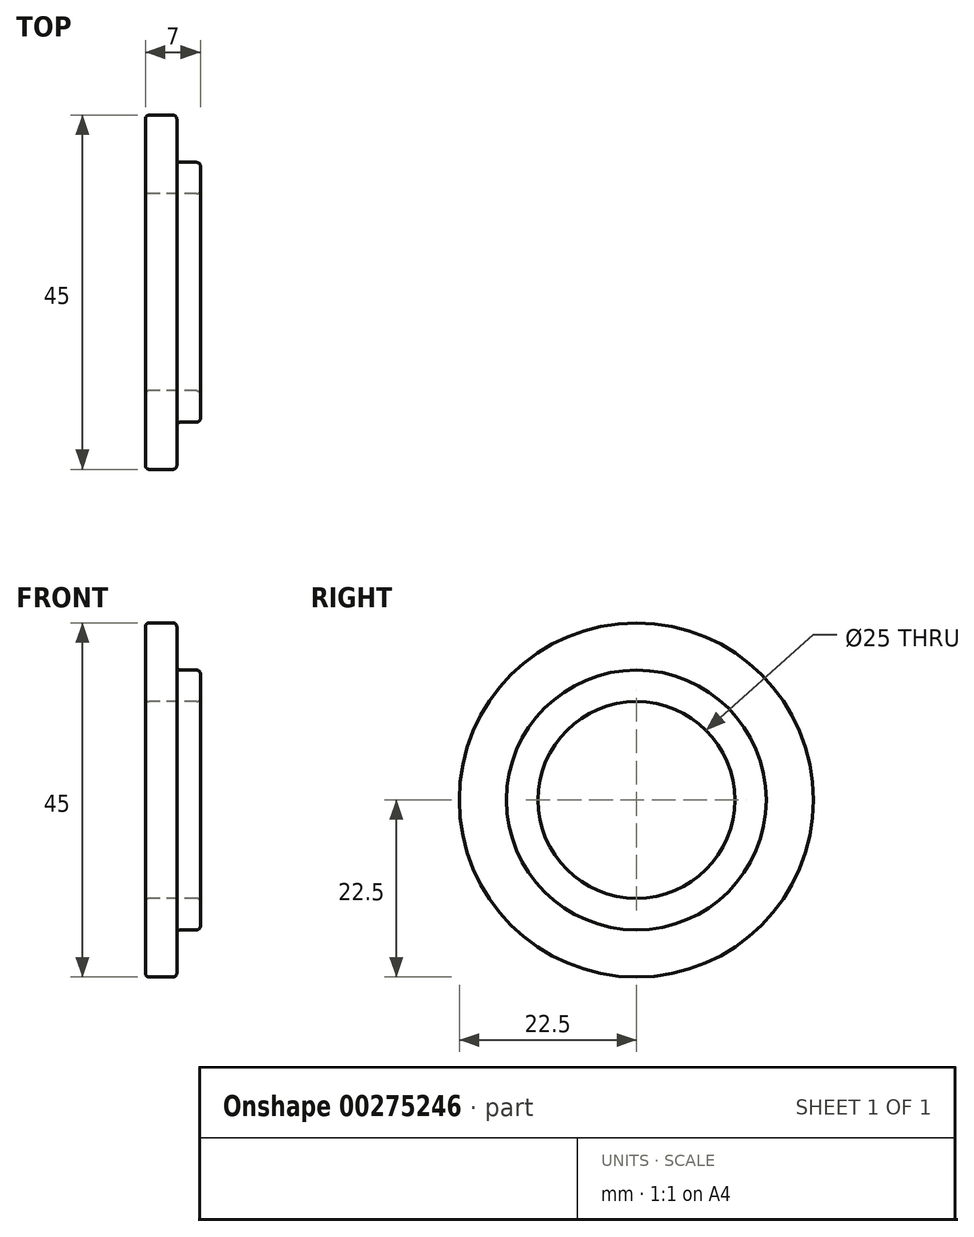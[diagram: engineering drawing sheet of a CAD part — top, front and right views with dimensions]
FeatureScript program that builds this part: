
annotation { "Feature Type Name" : "Feature", "Feature Type Description" : "" }
export const myFeature = defineFeature(function(context is Context, id is Id, definition is map)
    precondition{}
    {
        {
            var Q0;
            Q0=qCreatedBy(makeId("Front.planeOp"),FACE);
            var sketch = newSketch(context, id + "F0", { "sketchPlane" : qUnion([Q0])});
            skLineSegment(sketch, "E0", {"start": v(0, 0) * mm, "end": v(0, 10) * mm});
            skLineSegment(sketch, "E1", {"start": v(0, 10) * mm, "end": v(4, 10) * mm});
            skLineSegment(sketch, "E2", {"start": v(4, 10) * mm, "end": v(4, 4) * mm});
            skLineSegment(sketch, "E3", {"start": v(4, 4) * mm, "end": v(7, 4) * mm});
            skLineSegment(sketch, "E4", {"start": v(7, 4) * mm, "end": v(7, 0) * mm});
            skLineSegment(sketch, "E5", {"start": v(7, 0) * mm, "end": v(0, 0) * mm});
            skLineSegment(sketch, "E6", {"start": v(-26.03, -12.5) * mm, "end": v(32.28, -12.5) * mm, "construction": true});
            skSolve(sketch);
        }
        {
            var Q0;
            Q0 = qSketchRegion(id + "F0", true);
            var Q1;
            Q1=sQuery(id+"F0.wireOp",EDGE,"E6");
            revolve(context, id + "F1", {"entities" : qUnion([Q0]), "axis" : qUnion([Q1]), "revolveType" : RevolveType.FULL});
        }
        {
            var Q0;
            Q0=makeQuery(id+"F1.opRevolve","SWEPT_EDGE",EDGE,{"disambiguationData":[OSD([sQuery(id+"F0.wireOp",EDGE,"E3"),sQuery(id+"F0.wireOp",EDGE,"E4")])]});
            var Q1;
            Q1=makeQuery(id+"F1.opRevolve","SWEPT_EDGE",EDGE,{"disambiguationData":[OSD([sQuery(id+"F0.wireOp",EDGE,"E4"),sQuery(id+"F0.wireOp",EDGE,"E5")])]});
            var Q2;
            Q2=makeQuery(id+"F1.opRevolve","SWEPT_EDGE",EDGE,{"disambiguationData":[OSD([sQuery(id+"F0.wireOp",EDGE,"E1"),sQuery(id+"F0.wireOp",EDGE,"E2")])]});
            var Q3;
            Q3=makeQuery(id+"F1.opRevolve","SWEPT_EDGE",EDGE,{"disambiguationData":[OSD([sQuery(id+"F0.wireOp",EDGE,"E0"),sQuery(id+"F0.wireOp",EDGE,"E1")])]});
            var Q4;
            Q4=makeQuery(id+"F1.opRevolve","SWEPT_EDGE",EDGE,{"disambiguationData":[OSD([sQuery(id+"F0.wireOp",EDGE,"E0"),sQuery(id+"F0.wireOp",EDGE,"E5")])]});
            var Q5;
            Q5=makeQuery(id+"F1.opRevolve","SWEPT_EDGE",EDGE,{"disambiguationData":[OSD([sQuery(id+"F0.wireOp",EDGE,"E2"),sQuery(id+"F0.wireOp",EDGE,"E3")])]});
            fillet(context, id + "F2", {"entities" : qUnion([Q0, Q1, Q2, Q3, Q4, Q5]), "radius" : .5 * mm, "tangentPropagation" : true, "allowEdgeOverflow" : false});
        }
    });
